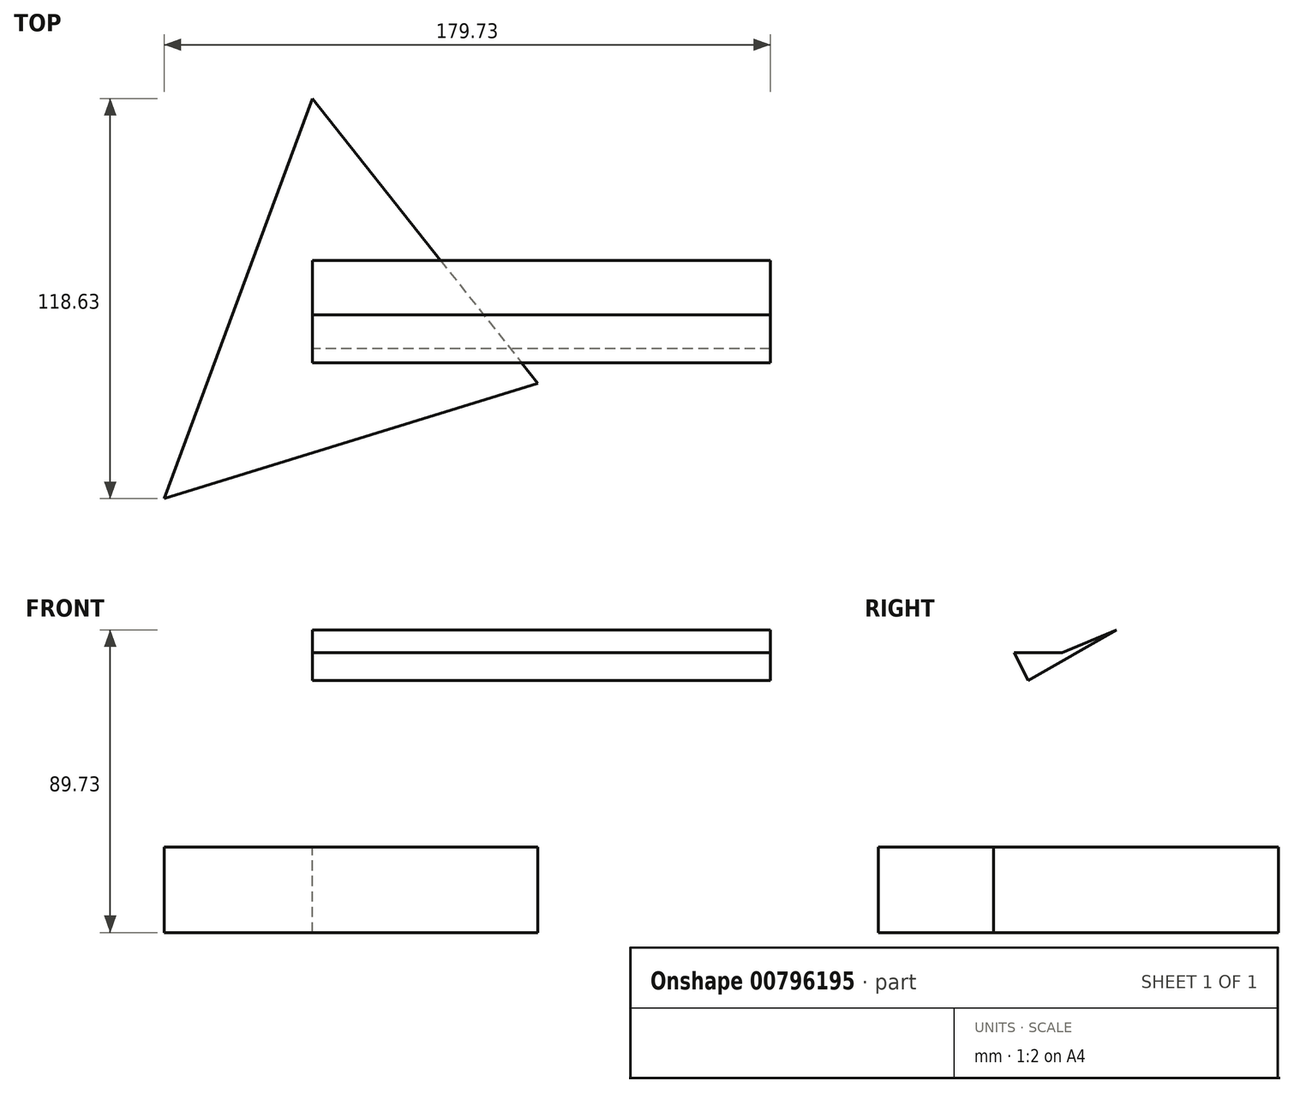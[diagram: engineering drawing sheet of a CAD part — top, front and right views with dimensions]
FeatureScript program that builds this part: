
annotation { "Feature Type Name" : "Feature", "Feature Type Description" : "" }
export const myFeature = defineFeature(function(context is Context, id is Id, definition is map)
    precondition{}
    {
        {
            var Q0;
            Q0=qCreatedBy(makeId("Top.planeOp"),FACE);
            var sketch = newSketch(context, id + "F0", { "sketchPlane" : qUnion([Q0])});
            skLineSegment(sketch, "E0", {"start": v(0, 74.19) * mm, "end": v(66.92, -10.27) * mm});
            skLineSegment(sketch, "E1", {"start": v(66.92, -10.27) * mm, "end": v(-43.9, -44.44) * mm});
            skLineSegment(sketch, "E2", {"start": v(-43.9, -44.44) * mm, "end": v(0, 74.19) * mm});
            skSolve(sketch);
        }
        {
            var Q0;
            Q0=makeQuery(id+"F0.imprint","IMPRINT",FACE,{"disambiguationData":[TD([[makeQuery(id+"F0.imprint","IMPRINT",EDGE,{"derivedFrom":sQuery(id+"F0.wireOp",EDGE,"E0")}),-1.0]])]});
            extrude(context, id + "F1", {"entities" : qUnion([Q0]), "oppositeDirection" : true, "depth" : 25.4 * mm, "offsetDistance" : 25.4 * mm});
        }
        {
            var Q0;
            Q0=qCreatedBy(makeId("Right.planeOp"),FACE);
            var sketch = newSketch(context, id + "F2", { "sketchPlane" : qUnion([Q0])});
            skLineSegment(sketch, "E3", {"start": v(26.23, 64.33) * mm, "end": v(10.09, 57.67) * mm});
            skLineSegment(sketch, "E4", {"start": v(10.09, 57.67) * mm, "end": v(-4.17, 57.67) * mm});
            skLineSegment(sketch, "E5", {"start": v(-4.17, 57.67) * mm, "end": v(0, 49.4) * mm});
            skLineSegment(sketch, "E6", {"start": v(0, 49.4) * mm, "end": v(26.23, 64.33) * mm});
            skSolve(sketch);
        }
        {
            var Q0;
            Q0=makeQuery(id+"F2.imprint","IMPRINT",FACE,{"disambiguationData":[TD([[makeQuery(id+"F2.imprint","IMPRINT",EDGE,{"derivedFrom":sQuery(id+"F2.wireOp",EDGE,"E3")}),1.0]])]});
            extrude(context, id + "F3", {"entities" : qUnion([Q0]), "depth" : 135.83 * mm, "offsetDistance" : 25.4 * mm});
        }
    });
